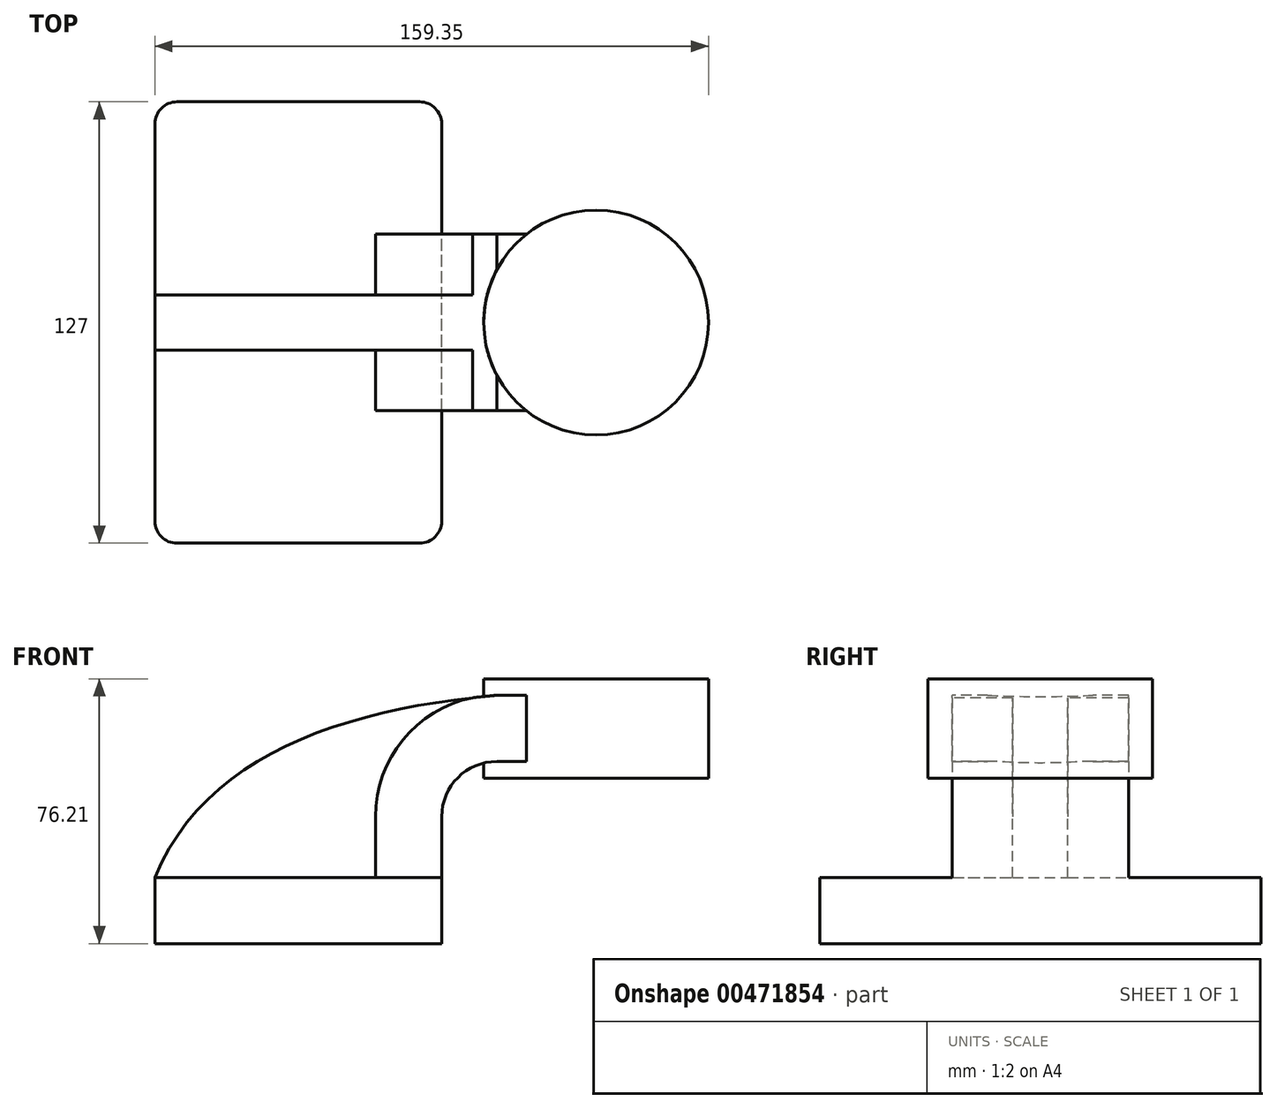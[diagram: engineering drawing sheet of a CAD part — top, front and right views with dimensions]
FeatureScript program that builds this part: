
annotation { "Feature Type Name" : "Feature", "Feature Type Description" : "" }
export const myFeature = defineFeature(function(context is Context, id is Id, definition is map)
    precondition{}
    {
        {
            var Q0;
            Q0=qCreatedBy(makeId("Front.planeOp"),FACE);
            var sketch = newSketch(context, id + "F0", { "sketchPlane" : qUnion([Q0])});
            skLineSegment(sketch, "E0.bottom", {"start": v(41.28, -9.52) * mm, "end": v(-41.28, -9.53) * mm});
            skLineSegment(sketch, "E0.top", {"start": v(41.28, 9.53) * mm, "end": v(-41.28, 9.52) * mm});
            skLineSegment(sketch, "E0.left", {"start": v(41.28, -9.52) * mm, "end": v(41.28, 9.53) * mm});
            skLineSegment(sketch, "E0.right", {"start": v(-41.28, -9.53) * mm, "end": v(-41.28, 9.52) * mm});
            skPoint(sketch, "E0.middle", {"position": v(0, 0) * mm});
            skLineSegment(sketch, "E1.bottom", {"start": v(118.07, 38.1) * mm, "end": v(67.27, 38.1) * mm});
            skLineSegment(sketch, "E1.top", {"start": v(118.07, 66.68) * mm, "end": v(67.27, 66.68) * mm});
            skLineSegment(sketch, "E1.left", {"start": v(118.07, 38.1) * mm, "end": v(118.07, 66.68) * mm});
            skLineSegment(sketch, "E1.right", {"start": v(67.27, 38.1) * mm, "end": v(67.27, 66.68) * mm});
            skPoint(sketch, "E1.middle", {"position": v(92.67, 52.39) * mm});
            skLineSegment(sketch, "E2", {"start": v(41.28, 9.53) * mm, "end": v(41.28, 27) * mm});
            skArc(sketch, "E3", {"start": v(41.28, 27) * mm, "mid": v(45.92, 38.23) * mm, "end": v(57.15, 42.88) * mm});
            skLineSegment(sketch, "E4", {"start": v(57.15, 42.88) * mm, "end": v(85.72, 42.88) * mm});
            skLineSegment(sketch, "E5.0", {"start": v(57.15, 61.93) * mm, "end": v(85.72, 61.93) * mm});
            skArc(sketch, "E5.1", {"start": v(22.23, 27) * mm, "mid": v(32.45, 51.7) * mm, "end": v(57.15, 61.93) * mm});
            skLineSegment(sketch, "E5.2", {"start": v(22.23, 9.53) * mm, "end": v(22.23, 27) * mm});
            skLineSegment(sketch, "E6", {"start": v(85.72, 61.93) * mm, "end": v(85.72, 42.88) * mm});
            skFitSpline(sketch, "E7", {"points": [v(-41.28, 9.52) * mm, v(57.15, 61.93) * mm], "startDerivative": vector(43.93, 106.75) * mm, "endDerivative": vector(130.54, 11.62) * mm});
            skLineSegment(sketch, "E8", {"start": v(85.72, 38.1) * mm, "end": v(85.72, 42.88) * mm});
            skLineSegment(sketch, "E9", {"start": v(85.72, 66.68) * mm, "end": v(85.72, 61.93) * mm});
            skSolve(sketch);
        }
        {
            var Q0;
            Q0=makeQuery(id+"F0.imprint","IMPRINT",FACE,{"disambiguationData":[TD([[makeQuery(id+"F0.imprint","IMPRINT",EDGE,{"derivedFrom":sQuery(id+"F0.wireOp",EDGE,"E0.bottom")}),-1.0]])]});
            extrude(context, id + "F1", {"entities" : qUnion([Q0]), "endBound" : BoundingType.SYMMETRIC, "depth" : 127 * mm});
        }
        {
            var Q0;
            {var subQ1=sQuery(id+"F0.wireOp",EDGE,"E2");Q0=makeQuery(id+"F0.imprint","IMPRINT",FACE,{"disambiguationData":[TD([[makeQuery(id+"F0.imprint","IMPRINT",EDGE,{"derivedFrom":subQ1}),1.0]])]});}
            var Q1;
            {var subQ5=sQuery(id+"F0.wireOp",EDGE,"E6");Q1=makeQuery(id+"F0.imprint","IMPRINT",FACE,{"disambiguationData":[TD([[makeQuery(id+"F0.imprint","IMPRINT",EDGE,{"derivedFrom":subQ5}),-1.0]])]});}
            extrude(context, id + "F2", {"entities" : qUnion([Q0, Q1]), "operationType" : NewBodyOperationType.ADD, "endBound" : BoundingType.SYMMETRIC, "depth" : 50.8 * mm});
        }
        {
            var Q0;
            {var subQ3=sQuery(id+"F0.wireOp",EDGE,"E5.2");Q0=makeQuery(id+"F0.imprint","IMPRINT",FACE,{"disambiguationData":[TD([[makeQuery(id+"F0.imprint","IMPRINT",EDGE,{"derivedFrom":subQ3}),1.0]])]});}
            extrude(context, id + "F3", {"entities" : qUnion([Q0]), "operationType" : NewBodyOperationType.ADD, "endBound" : BoundingType.SYMMETRIC, "depth" : 15.88 * mm});
        }
        {
            var Q0;
            {var subQ0=sQuery(id+"F0.wireOp",EDGE,"E1.left");Q0=makeQuery(id+"F0.imprint","IMPRINT",FACE,{"disambiguationData":[TD([[makeQuery(id+"F0.imprint","IMPRINT",EDGE,{"derivedFrom":subQ0}),1.0]])]});}
            var Q1;
            Q1=sQuery(id+"F0.wireOp",EDGE,"E6");
            revolve(context, id + "F4", {"operationType" : NewBodyOperationType.ADD, "entities" : qUnion([Q0]), "axis" : qUnion([Q1]), "revolveType" : RevolveType.FULL});
        }
        {
            var Q0;
            Q0=makeQuery(id+"F1.opExtrude","CAP_EDGE",EDGE,{"disambiguationData":[OSD([sQuery(id+"F0.wireOp",EDGE,"E0.right")])],"isStart":false});
            var Q1;
            Q1=makeQuery(id+"F1.opExtrude","CAP_EDGE",EDGE,{"disambiguationData":[OSD([sQuery(id+"F0.wireOp",EDGE,"E0.left")])],"isStart":false});
            var Q2;
            Q2=makeQuery(id+"F1.opExtrude","CAP_EDGE",EDGE,{"disambiguationData":[OSD([sQuery(id+"F0.wireOp",EDGE,"E0.left")])],"isStart":true});
            var Q3;
            Q3=makeQuery(id+"F1.opExtrude","CAP_EDGE",EDGE,{"disambiguationData":[OSD([sQuery(id+"F0.wireOp",EDGE,"E0.right")])],"isStart":true});
            fillet(context, id + "F5", {"entities" : qUnion([Q0, Q1, Q2, Q3]), "radius" : 6.35 * mm, "tangentPropagation" : true, "allowEdgeOverflow" : false});
        }
    });
